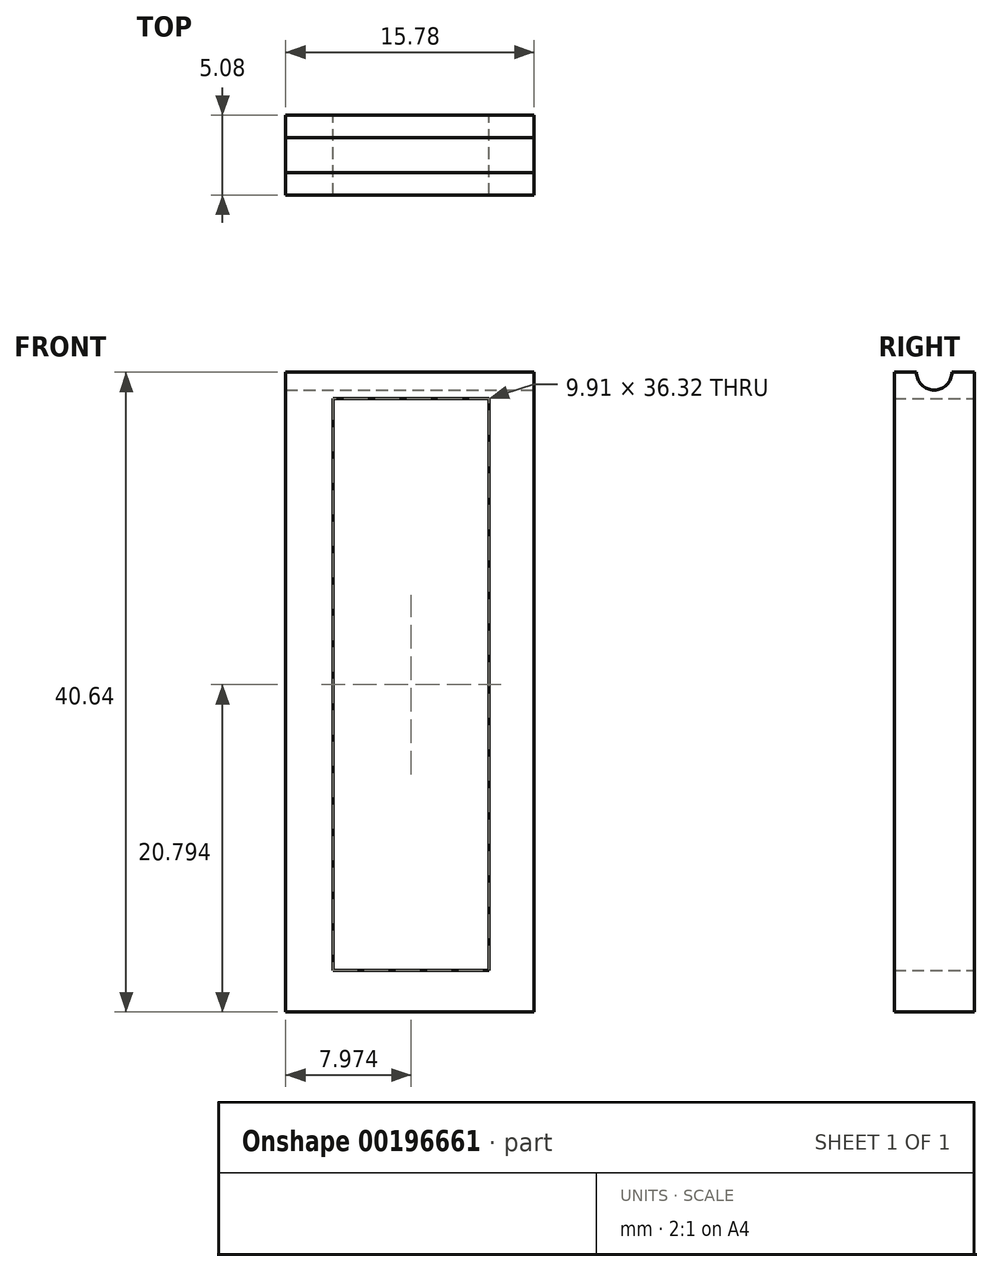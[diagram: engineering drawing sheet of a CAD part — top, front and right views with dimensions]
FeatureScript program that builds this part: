
annotation { "Feature Type Name" : "Feature", "Feature Type Description" : "" }
export const myFeature = defineFeature(function(context is Context, id is Id, definition is map)
    precondition{}
    {
        {
            var Q0;
            Q0=qCreatedBy(makeId("Front.planeOp"),FACE);
            var sketch = newSketch(context, id + "F0", { "sketchPlane" : qUnion([Q0])});
            skLineSegment(sketch, "E0", {"start": v(-4.87, 0) * mm, "end": v(0, 0) * mm});
            skLineSegment(sketch, "E1.bottom", {"start": v(7.9, 0) * mm, "end": v(-7.9, 0) * mm});
            skLineSegment(sketch, "E1.top", {"start": v(7.9, 40.64) * mm, "end": v(-7.9, 40.64) * mm});
            skLineSegment(sketch, "E2", {"start": v(-7.9, 40.64) * mm, "end": v(-7.9, 0) * mm});
            skLineSegment(sketch, "E3", {"start": v(7.9, 40.64) * mm, "end": v(7.9, 0) * mm});
            skLineSegment(sketch, "E4.bottom", {"start": v(5.04, 2.63) * mm, "end": v(-4.87, 2.63) * mm});
            skLineSegment(sketch, "E4.top", {"start": v(5.04, 38.96) * mm, "end": v(-4.87, 38.96) * mm});
            skLineSegment(sketch, "E4.left", {"start": v(5.04, 2.63) * mm, "end": v(5.04, 38.96) * mm});
            skLineSegment(sketch, "E4.right", {"start": v(-4.87, 2.63) * mm, "end": v(-4.87, 38.96) * mm});
            skSolve(sketch);
        }
        {
            var Q0;
            Q0 = qSketchRegion(id + "F0", true);
            extrude(context, id + "F1", {"entities" : qUnion([Q0]), "depth" : 5.08 * mm});
        }
        {
            var Q0;
            Q0=makeQuery(id+"F1.opExtrude","SWEPT_FACE",FACE,{"disambiguationData":[OSD([sQuery(id+"F0.wireOp",EDGE,"E3")])]});
            var sketch = newSketch(context, id + "F2", { "sketchPlane" : qUnion([Q0])});
            skPoint(sketch, "E5", {"position": v(-2.54, 40.64) * mm});
            skCircle(sketch, "E6", {"center": v(-2.54, 40.64) * mm, "radius": 1.12 * mm});
            skSolve(sketch);
        }
        {
            var Q0;
            Q0 = qSketchRegion(id + "F2", true);
            extrude(context, id + "F3", {"entities" : qUnion([Q0]), "operationType" : NewBodyOperationType.REMOVE, "oppositeDirection" : true, "depth" : 25.4 * mm});
        }
    });
